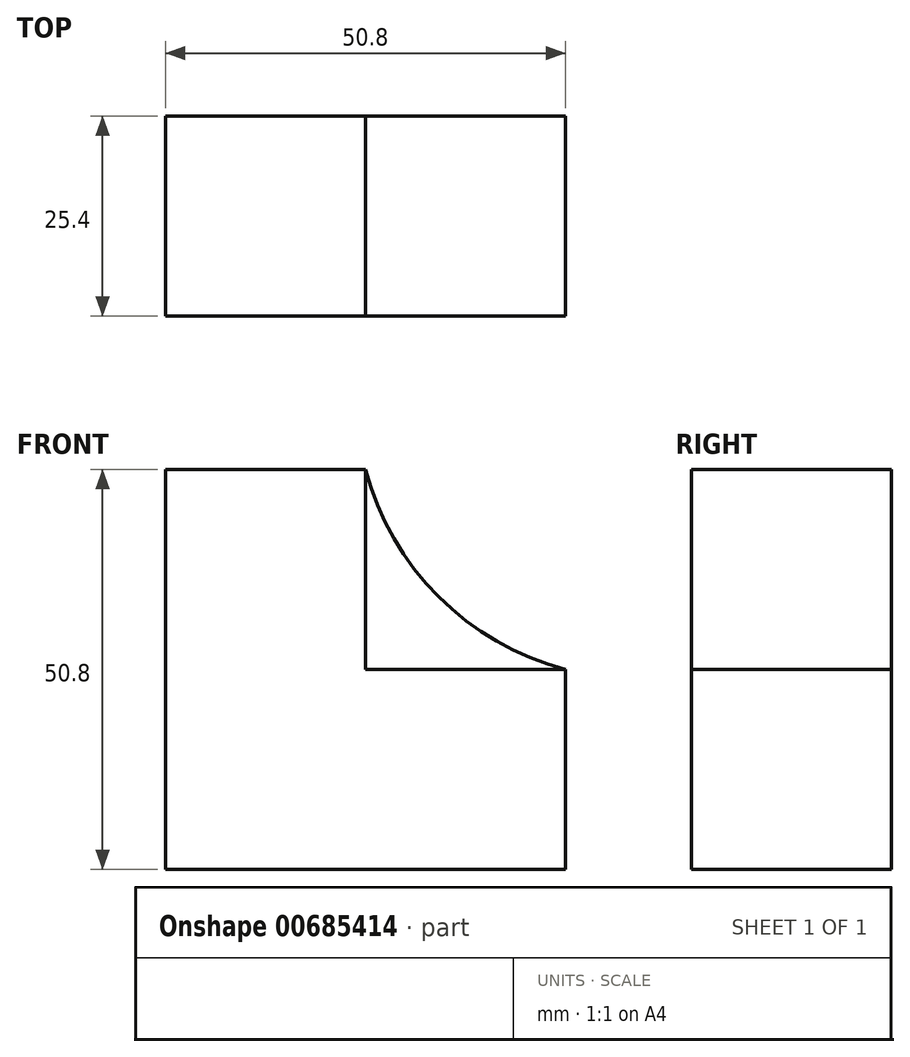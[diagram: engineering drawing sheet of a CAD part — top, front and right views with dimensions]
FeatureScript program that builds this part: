
annotation { "Feature Type Name" : "Feature", "Feature Type Description" : "" }
export const myFeature = defineFeature(function(context is Context, id is Id, definition is map)
    precondition{}
    {
        {
            var Q0;
            Q0=qCreatedBy(makeId("Front.planeOp"),FACE);
            var sketch = newSketch(context, id + "F0", { "sketchPlane" : qUnion([Q0])});
            skLineSegment(sketch, "E0", {"start": v(0, 0) * mm, "end": v(0, 50.8) * mm});
            skLineSegment(sketch, "E1", {"start": v(0, 50.8) * mm, "end": v(25.4, 50.8) * mm});
            skLineSegment(sketch, "E2", {"start": v(25.4, 50.8) * mm, "end": v(25.4, 25.4) * mm});
            skLineSegment(sketch, "E3", {"start": v(25.4, 25.4) * mm, "end": v(50.8, 25.4) * mm});
            skLineSegment(sketch, "E4", {"start": v(50.8, 25.4) * mm, "end": v(50.8, 0) * mm});
            skLineSegment(sketch, "E5", {"start": v(50.8, 0) * mm, "end": v(0, 0) * mm});
            skSolve(sketch);
        }
        {
            var Q0;
            Q0=makeQuery(id+"F0.imprint","IMPRINT",FACE,{"disambiguationData":[TD([[makeQuery(id+"F0.imprint","IMPRINT",EDGE,{"derivedFrom":sQuery(id+"F0.wireOp",EDGE,"E0")}),-1.0]])]});
            extrude(context, id + "F1", {"entities" : qUnion([Q0]), "depth" : 25.4 * mm, "offsetDistance" : 25.4 * mm});
        }
        {
            var Q0;
            Q0=makeQuery(id+"F1.opExtrude","SWEPT_EDGE",EDGE,{"disambiguationData":[OSD([sQuery(id+"F0.wireOp",EDGE,"E2"),sQuery(id+"F0.wireOp",EDGE,"E3")])]});
            fillet(context, id + "F2", {"entities" : qUnion([Q0]), "radius" : 35.57 * mm, "tangentPropagation" : true, "allowEdgeOverflow" : false});
        }
        {
            var Q0;
            Q0=makeQuery(id+"F0.imprint","IMPRINT",FACE,{"disambiguationData":[TD([[makeQuery(id+"F0.imprint","IMPRINT",EDGE,{"derivedFrom":sQuery(id+"F0.wireOp",EDGE,"E0")}),-1.0]])]});
            extrude(context, id + "F3", {"entities" : qUnion([Q0]), "depth" : 25.4 * mm, "offsetDistance" : 25.4 * mm});
        }
    });
